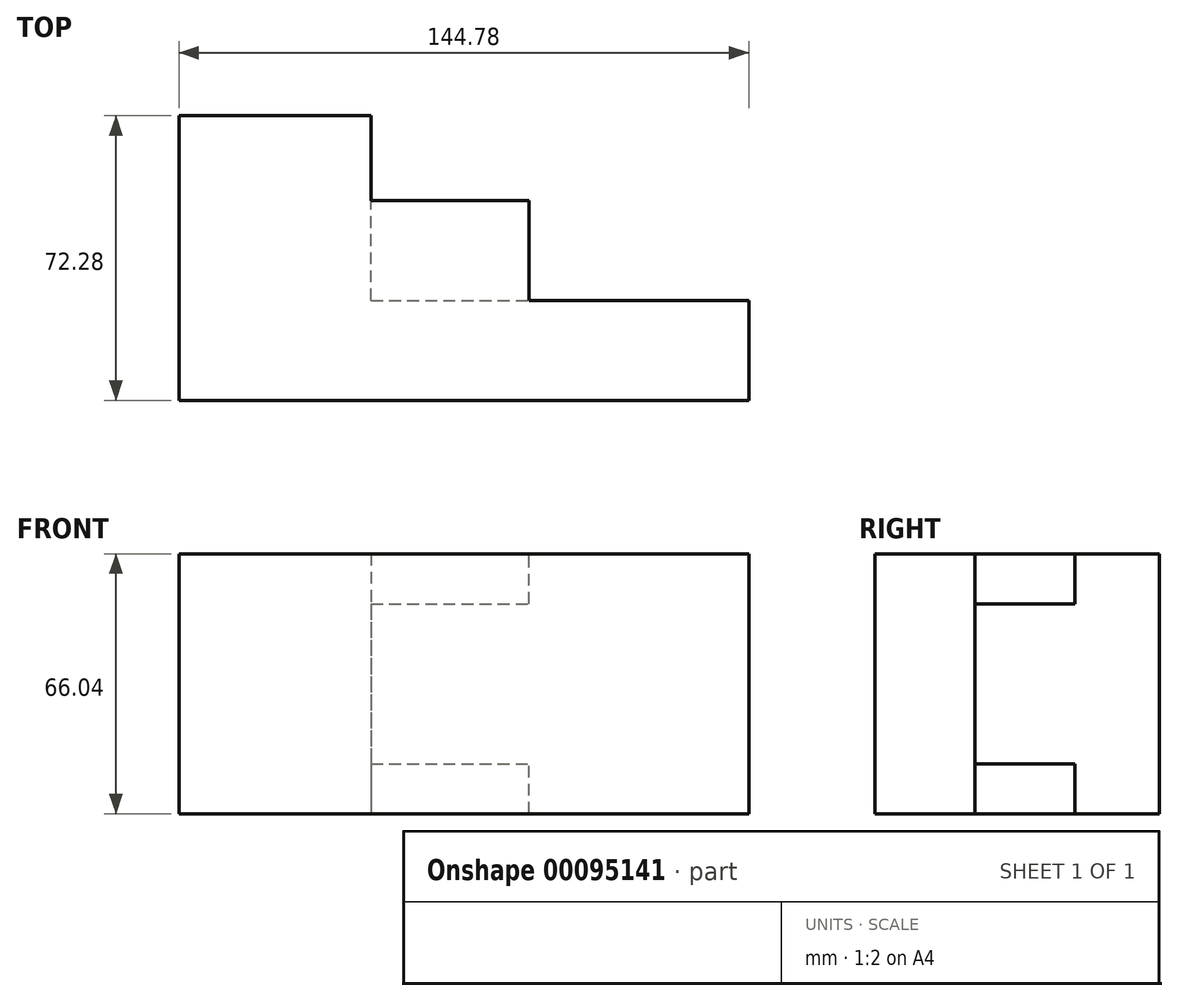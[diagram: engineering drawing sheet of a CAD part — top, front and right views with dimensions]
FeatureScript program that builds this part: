
annotation { "Feature Type Name" : "Feature", "Feature Type Description" : "" }
export const myFeature = defineFeature(function(context is Context, id is Id, definition is map)
    precondition{}
    {
        {
            var Q0;
            Q0=qCreatedBy(makeId("Front.planeOp"),FACE);
            var sketch = newSketch(context, id + "F0", { "sketchPlane" : qUnion([Q0])});
            skLineSegment(sketch, "E0.bottom", {"start": v(-73.18, 25.3) * mm, "end": v(71.6, 25.3) * mm});
            skLineSegment(sketch, "E0.top", {"start": v(-73.18, -40.75) * mm, "end": v(71.6, -40.75) * mm});
            skLineSegment(sketch, "E0.left", {"start": v(-73.18, 25.3) * mm, "end": v(-73.18, -40.75) * mm});
            skLineSegment(sketch, "E0.right", {"start": v(71.6, 25.3) * mm, "end": v(71.6, -40.75) * mm});
            skSolve(sketch);
        }
        {
            var Q0;
            Q0=makeQuery(id+"F0.imprint","IMPRINT",FACE,{"disambiguationData":[TD([[makeQuery(id+"F0.imprint","IMPRINT",EDGE,{"derivedFrom":sQuery(id+"F0.wireOp",EDGE,"E0.bottom")}),-1.0]])]});
            extrude(context, id + "F1", {"entities" : qUnion([Q0]), "depth" : 25.4 * mm});
        }
        {
            var Q0;
            Q0=qCreatedBy(makeId("Front.planeOp"),FACE);
            var sketch = newSketch(context, id + "F2", { "sketchPlane" : qUnion([Q0])});
            skLineSegment(sketch, "E1.bottom", {"start": v(-73.18, -40.75) * mm, "end": v(15.72, -40.75) * mm});
            skLineSegment(sketch, "E1.top", {"start": v(-73.18, -28.05) * mm, "end": v(15.72, -28.05) * mm});
            skLineSegment(sketch, "E1.left", {"start": v(-73.18, -40.75) * mm, "end": v(-73.18, -28.05) * mm});
            skLineSegment(sketch, "E1.right", {"start": v(15.72, -40.75) * mm, "end": v(15.72, -28.05) * mm});
            skLineSegment(sketch, "E2.bottom", {"start": v(-73.18, 12.6) * mm, "end": v(15.72, 12.6) * mm});
            skLineSegment(sketch, "E2.top", {"start": v(-73.18, 25.3) * mm, "end": v(15.72, 25.3) * mm});
            skLineSegment(sketch, "E2.left", {"start": v(-73.18, 12.6) * mm, "end": v(-73.18, 25.3) * mm});
            skLineSegment(sketch, "E2.right", {"start": v(15.72, 12.6) * mm, "end": v(15.72, 25.3) * mm});
            skSolve(sketch);
        }
        {
            var Q0;
            Q0 = qSketchRegion(id + "F2", true);
            extrude(context, id + "F3", {"entities" : qUnion([Q0]), "operationType" : NewBodyOperationType.ADD, "oppositeDirection" : true, "depth" : 25.4 * mm});
        }
        {
            var Q0;
            Q0=qCreatedBy(makeId("Front.planeOp"),FACE);
            var sketch = newSketch(context, id + "F4", { "sketchPlane" : qUnion([Q0])});
            skLineSegment(sketch, "E3.bottom", {"start": v(-24.38, 25.3) * mm, "end": v(-73.18, 25.3) * mm});
            skLineSegment(sketch, "E3.top", {"start": v(-24.38, -40.75) * mm, "end": v(-73.18, -40.75) * mm});
            skLineSegment(sketch, "E3.left", {"start": v(-24.38, 25.3) * mm, "end": v(-24.38, -40.75) * mm});
            skLineSegment(sketch, "E3.right", {"start": v(-73.18, 25.3) * mm, "end": v(-73.18, -40.75) * mm});
            skSolve(sketch);
        }
        {
            var Q0;
            Q0 = qSketchRegion(id + "F4", true);
            extrude(context, id + "F5", {"entities" : qUnion([Q0]), "operationType" : NewBodyOperationType.ADD, "oppositeDirection" : true, "depth" : 46.88 * mm});
        }
    });
